# Revit family: Paper_Towel_Dispenser-Waste_Receptacle-Recessed-Bobrick-ClassicSeries-B-39747.rfaxxx
name_source: partatom
category: Specialty Equipment
units: mm (PartAtom-declared; Revit-internal decimal feet)

## family parameters
Cut with Voids When Loaded = Yes
Host = Face
OmniClass Number = 23.40.20.21.17
OmniClass Title = Paper Towel Dispensers, Disposal Units
Part Type = Normal
Room Calculation Point = No
Round Connector Dimension = Use Diameter
Shared = Yes

## types (1)
- B-39747
    368-60 Waste Receptacle = No
    3944-134 LinerMate® = No
    3944-152 Folded Towel Dispenser Module = No
    3961-50 Mechanical (Non-Automatic) Universal Touch-Free Roll Towel Dispenser Module = No
    3974-57 AC External Adapter (6V) = No
    ADA Compliant = Yes
    ADA/ICC = Yes
    Assembly Code = C1030200
    Battery Operated = Yes
    CBC = No
    Cabinet Material = Stainless Steel-Bobrick-Satin
    Capacity = 18-gallon (68 L)
    Default Elevation = 0"
    Description = Recessed Convertible Automatic, Universal Roll Towel Dispenser/Waste Receptacle
    Door Material = Stainless Steel-Bobrick-Satin
    Flange Material = Stainless Steel-Bobrick-Satin
    Height = 56"
    Installation Type = Wall Mounted
    Manufacturer = Bobrick
    Material = Stainless Steel-Bobrick-Satin
    Model = B-39747
    Mounting Height = 60"
    Mounting Height Constraint = 64 7/8"
    Operation = Electronic Sensor
    Product Page URL = https://www.bobrick.com
    Revised Date = 01/11/2023
    Rough Wall Opening = 16"
    URL = http://www.bobrick.com
    Voltage Nominal = 0 V
    Wast Receptacle Material = Stainless Steel-Bobrick-Satin
    Width = 17 3/16"

## geometry (parser evidence)
native form markers: Sweep x2
no freeform markers — native parametric forms only
